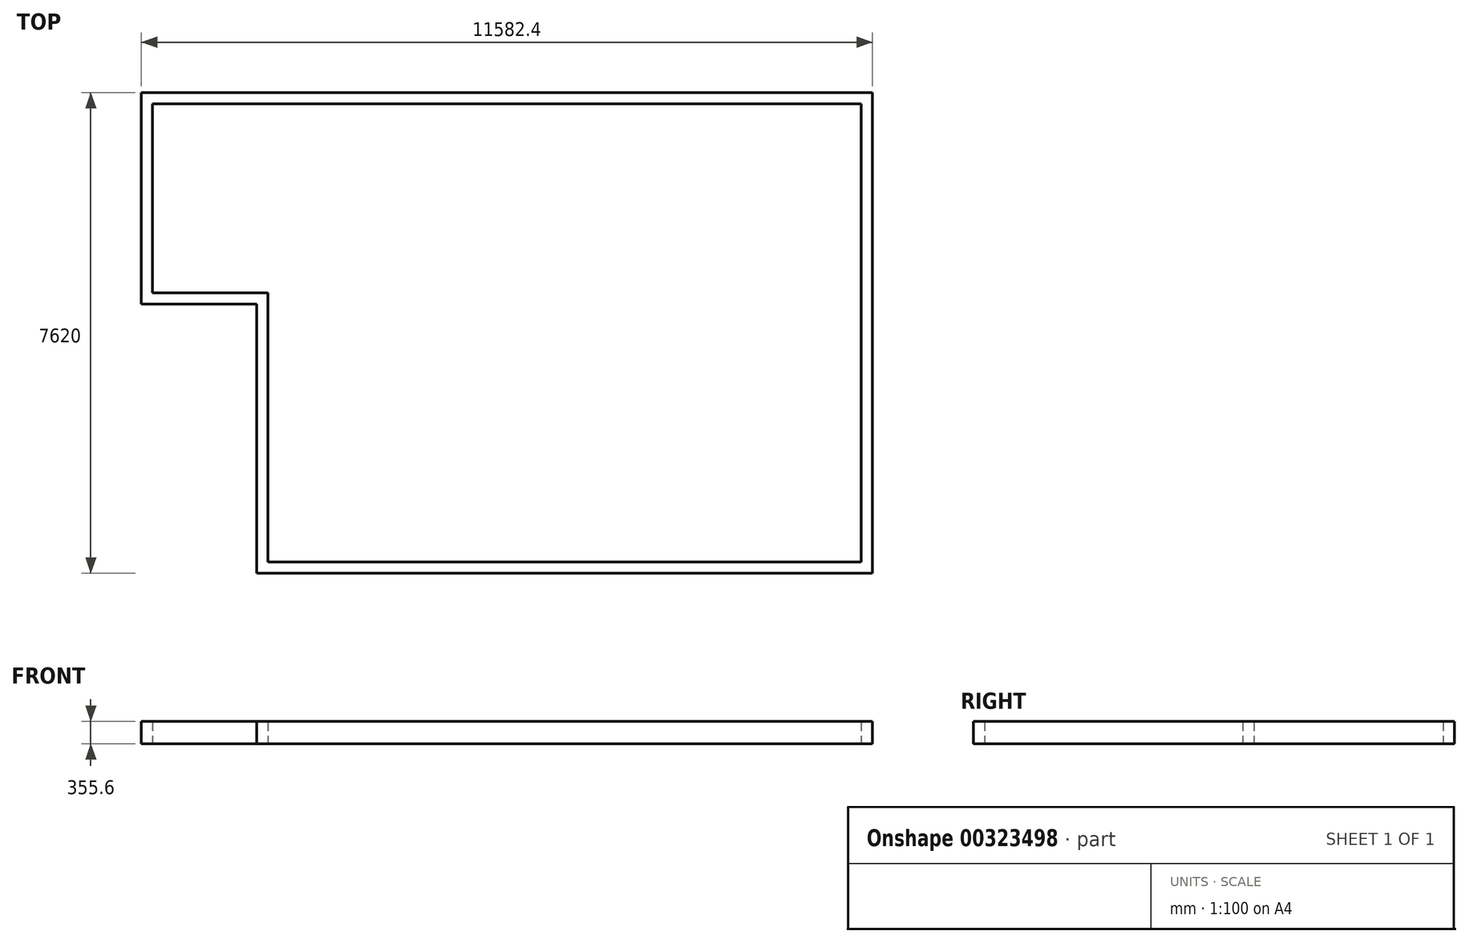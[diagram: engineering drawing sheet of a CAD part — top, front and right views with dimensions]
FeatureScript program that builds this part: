
annotation { "Feature Type Name" : "Feature", "Feature Type Description" : "" }
export const myFeature = defineFeature(function(context is Context, id is Id, definition is map)
    precondition{}
    {
        {
            var Q0;
            Q0=qCreatedBy(makeId("Top.planeOp"),FACE);
            var sketch = newSketch(context, id + "F0", { "sketchPlane" : qUnion([Q0])});
            skLineSegment(sketch, "E0", {"start": v(0, 0) * mm, "end": v(-9753.6, 0) * mm});
            skLineSegment(sketch, "E1", {"start": v(0, 0) * mm, "end": v(0, 7620) * mm});
            skLineSegment(sketch, "E2", {"start": v(0, 7620) * mm, "end": v(-11582.4, 7620) * mm});
            skLineSegment(sketch, "E3", {"start": v(-11582.4, 7620) * mm, "end": v(-11582.4, 4267.2) * mm});
            skLineSegment(sketch, "E4", {"start": v(-11582.4, 4267.2) * mm, "end": v(-9753.6, 4267.2) * mm});
            skLineSegment(sketch, "E5", {"start": v(-9753.6, 4267.2) * mm, "end": v(-9753.6, 0) * mm});
            skLineSegment(sketch, "E6.0", {"start": v(-11404.6, 4445) * mm, "end": v(-9575.8, 4445) * mm});
            skLineSegment(sketch, "E6.1", {"start": v(-177.8, 177.8) * mm, "end": v(-9575.8, 177.8) * mm});
            skLineSegment(sketch, "E6.2", {"start": v(-177.8, 177.8) * mm, "end": v(-177.8, 7442.2) * mm});
            skLineSegment(sketch, "E6.3", {"start": v(-9575.8, 4445) * mm, "end": v(-9575.8, 177.8) * mm});
            skLineSegment(sketch, "E6.4", {"start": v(-177.8, 7442.2) * mm, "end": v(-11404.6, 7442.2) * mm});
            skLineSegment(sketch, "E6.5", {"start": v(-11404.6, 7442.2) * mm, "end": v(-11404.6, 4445) * mm});
            skSolve(sketch);
        }
        {
            var Q0;
            Q0=makeQuery(id+"F0.imprint","IMPRINT",FACE,{"disambiguationData":[TD([[makeQuery(id+"F0.imprint","IMPRINT",EDGE,{"derivedFrom":sQuery(id+"F0.wireOp",EDGE,"E0")}),-1.0]])]});
            extrude(context, id + "F1", {"entities" : qUnion([Q0]), "depth" : 355.6 * mm});
        }
    });
